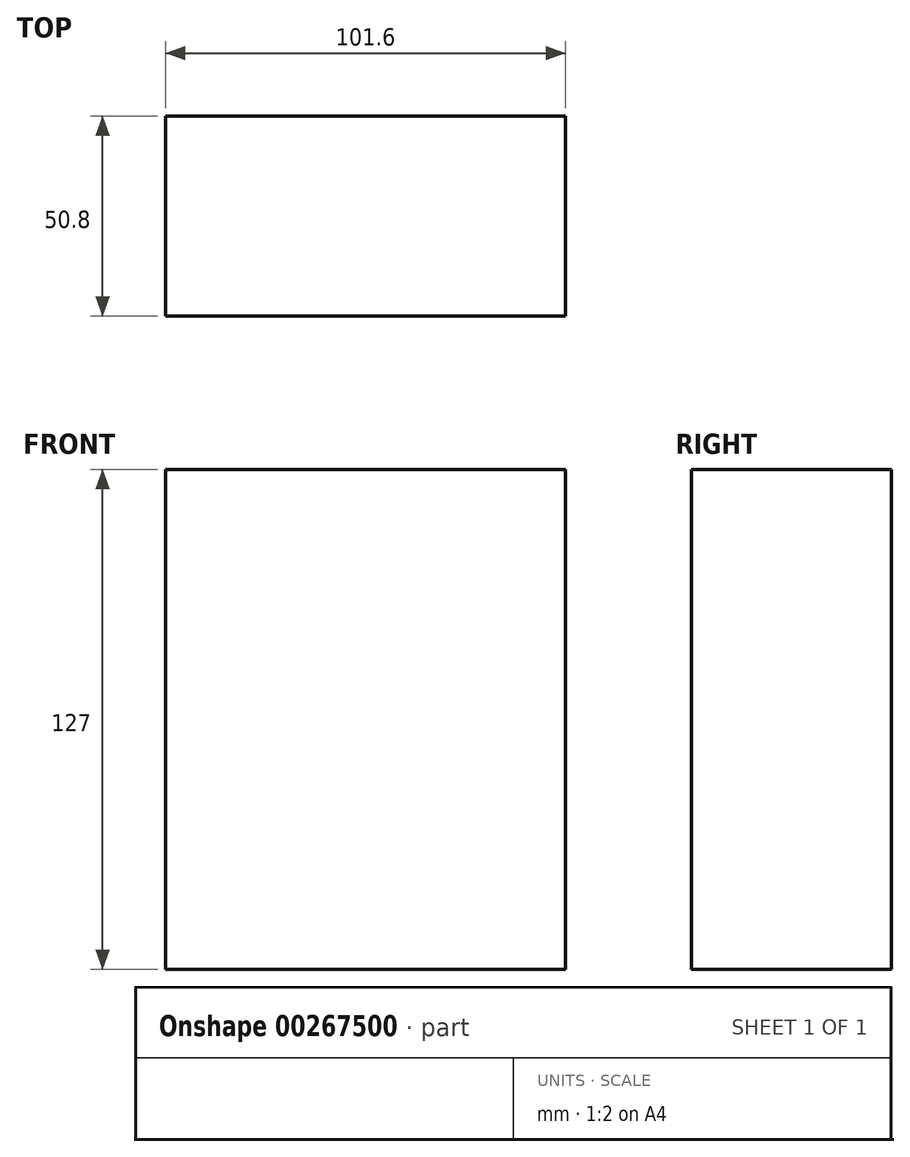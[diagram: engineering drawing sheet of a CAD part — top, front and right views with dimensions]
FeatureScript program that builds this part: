
annotation { "Feature Type Name" : "Feature", "Feature Type Description" : "" }
export const myFeature = defineFeature(function(context is Context, id is Id, definition is map)
    precondition{}
    {
        {
            var Q0;
            Q0=qCreatedBy(makeId("Front.planeOp"),FACE);
            var sketch = newSketch(context, id + "F0", { "sketchPlane" : qUnion([Q0])});
            skLineSegment(sketch, "E0.bottom", {"start": v(50.8, -63.5) * mm, "end": v(-50.8, -63.5) * mm});
            skLineSegment(sketch, "E0.top", {"start": v(50.8, 63.5) * mm, "end": v(-50.8, 63.5) * mm});
            skLineSegment(sketch, "E0.left", {"start": v(50.8, -63.5) * mm, "end": v(50.8, 63.5) * mm});
            skLineSegment(sketch, "E0.right", {"start": v(-50.8, -63.5) * mm, "end": v(-50.8, 63.5) * mm});
            skPoint(sketch, "E0.middle", {"position": v(0, 0) * mm});
            skSolve(sketch);
        }
        {
            var Q0;
            Q0 = qSketchRegion(id + "F0", true);
            extrude(context, id + "F1", {"entities" : qUnion([Q0]), "depth" : 50.8 * mm});
        }
    });
